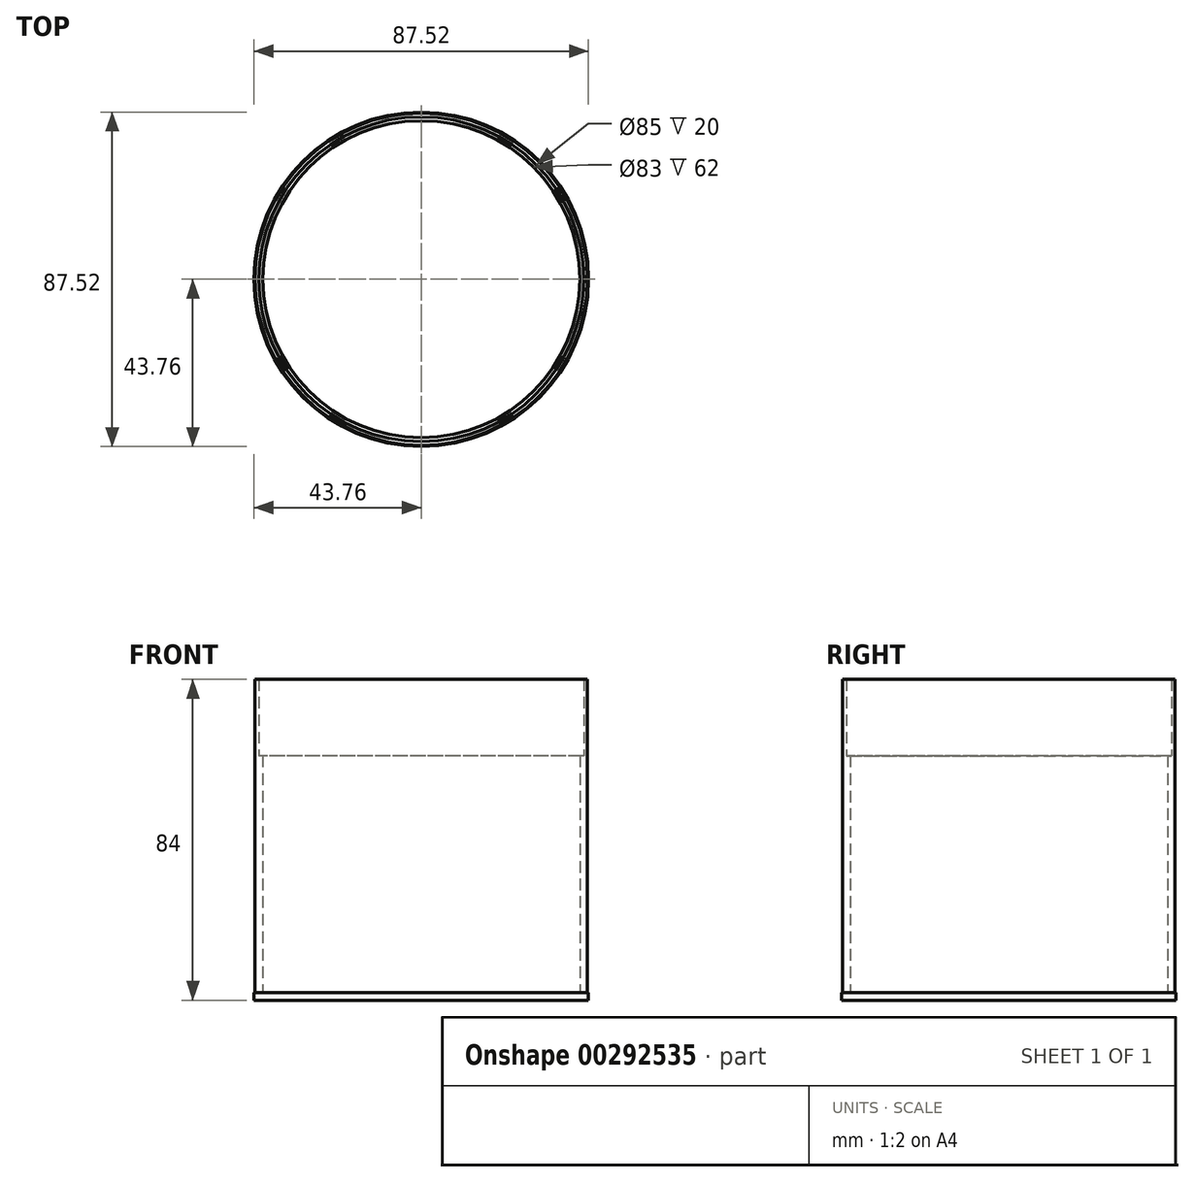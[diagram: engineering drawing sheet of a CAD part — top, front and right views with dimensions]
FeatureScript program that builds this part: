
annotation { "Feature Type Name" : "Feature", "Feature Type Description" : "" }
export const myFeature = defineFeature(function(context is Context, id is Id, definition is map)
    precondition{}
    {
        {
            var Q0;
            Q0=qCreatedBy(makeId("Top.planeOp"),FACE);
            var sketch = newSketch(context, id + "F0", { "sketchPlane" : qUnion([Q0])});
            skCircle(sketch, "E0", {"center": v(0, 0) * mm, "radius": 41.5 * mm});
            skCircle(sketch, "E1.0", {"center": v(0, 0) * mm, "radius": 43.5 * mm});
            skSolve(sketch);
        }
        {
            var Q0;
            Q0=makeQuery(id+"F0.imprint","IMPRINT",FACE,{"disambiguationData":[TD([[makeQuery(id+"F0.imprint","IMPRINT",EDGE,{"derivedFrom":sQuery(id+"F0.wireOp",EDGE,"E0")}),-1.0]])]});
            extrude(context, id + "F1", {"entities" : qUnion([Q0]), "depth" : 82 * mm});
        }
        {
            var Q0;
            Q0=qCreatedBy(makeId("Top.planeOp"),FACE);
            var sketch = newSketch(context, id + "F2", { "sketchPlane" : qUnion([Q0])});
            skCircle(sketch, "E2", {"center": v(0, 0) * mm, "radius": 43.76 * mm});
            skSolve(sketch);
        }
        {
            var Q0;
            Q0 = qSketchRegion(id + "F2", true);
            extrude(context, id + "F3", {"entities" : qUnion([Q0]), "operationType" : NewBodyOperationType.ADD, "oppositeDirection" : true, "depth" : 2 * mm});
        }
        {
            var Q0;
            Q0=qCreatedBy(makeId("Top.planeOp"),FACE);
            cPlane(context, id + "F4", {"entities" : qUnion([Q0]), "cplaneType" : CPlaneType.OFFSET, "offset" : 62 * mm, "width" : 152.4 * mm, "height" : 152.4 * mm});
        }
        {
            var Q0;
            Q0=qCreatedBy(id+"F4.planeOp",FACE);
            var sketch = newSketch(context, id + "F5", { "sketchPlane" : qUnion([Q0])});
            skCircle(sketch, "E3", {"center": v(0, 0) * mm, "radius": 43.5 * mm});
            skCircle(sketch, "E4.0", {"center": v(0, 0) * mm, "radius": 42.5 * mm});
            skCircle(sketch, "E5.0", {"center": v(0, 0) * mm, "radius": 41.5 * mm});
            skSolve(sketch);
        }
        {
            var Q0;
            Q0=makeQuery(id+"F5.imprint","IMPRINT",FACE,{"disambiguationData":[TD([[makeQuery(id+"F5.imprint","IMPRINT",EDGE,{"derivedFrom":sQuery(id+"F5.wireOp",EDGE,"E4.0")}),1.0]])]});
            extrude(context, id + "F6", {"entities" : qUnion([Q0]), "operationType" : NewBodyOperationType.REMOVE, "depth" : 20 * mm});
        }
    });
